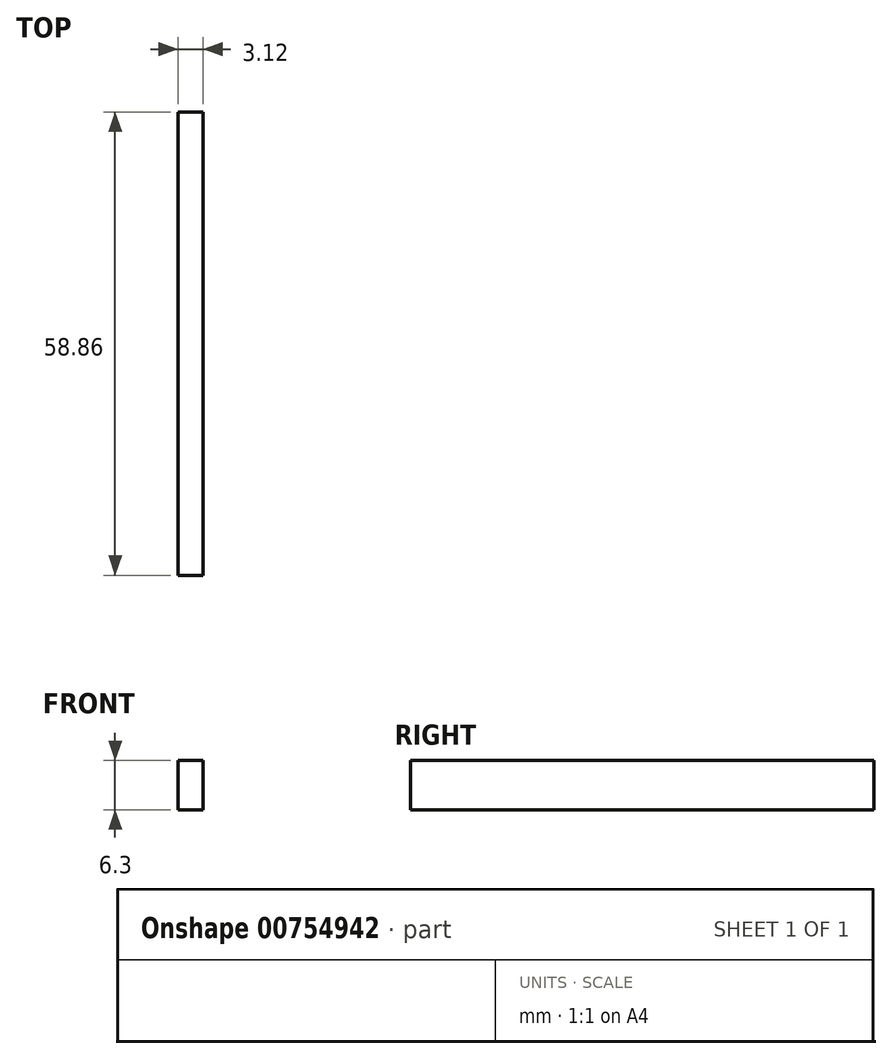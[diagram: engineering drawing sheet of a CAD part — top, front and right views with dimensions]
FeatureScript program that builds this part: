
annotation { "Feature Type Name" : "Feature", "Feature Type Description" : "" }
export const myFeature = defineFeature(function(context is Context, id is Id, definition is map)
    precondition{}
    {
        {
            var Q0;
            Q0=qCreatedBy(makeId("Right.planeOp"),FACE);
            var sketch = newSketch(context, id + "F0", { "sketchPlane" : qUnion([Q0])});
            skLineSegment(sketch, "E0.bottom", {"start": v(-58.86, 0) * mm, "end": v(0, 0) * mm});
            skLineSegment(sketch, "E0.top", {"start": v(-58.86, 6.3) * mm, "end": v(0, 6.3) * mm});
            skLineSegment(sketch, "E0.left", {"start": v(-58.86, 0) * mm, "end": v(-58.86, 6.3) * mm});
            skLineSegment(sketch, "E0.right", {"start": v(0, 0) * mm, "end": v(0, 6.3) * mm});
            skSolve(sketch);
        }
        {
            var Q0;
            Q0 = qSketchRegion(id + "F0", true);
            extrude(context, id + "F1", {"entities" : qUnion([Q0]), "oppositeDirection" : true, "depth" : 3.12 * mm, "offsetDistance" : 25.4 * mm});
        }
    });
